FCSTD DOCUMENT  (FreeCAD 0.19R24366 (Git))
Label: Amplifier box insulating mounting flange
License: All rights reserved
LicenseURL: http://en.wikipedia.org/wiki/All_rights_reserved
objects: Sketcher::SketchObject×1, PartDesign::Body×1
note: 2 computed .brp shape members not serialized (recipe doc carries the construction recipe); baked Part::Feature solids carry a one-line shape summary decoded from their .brp

FEATURE [Sketcher::SketchObject] Sketch
  FullyConstrained = true
  MapMode = 5
  Support = -> [XY_Plane]
  sketch-geometry (27):
    g0: LineSegment StartX=-40 StartY=53.5 StartZ=0 EndX=-40 EndY=-53.5 EndZ=0
    g1: LineSegment StartX=40 StartY=53.5 StartZ=0 EndX=40 EndY=-53.5 EndZ=0
    g2: LineSegment StartX=-40 StartY=53.5 StartZ=0 EndX=40 EndY=53.5 EndZ=0
    g3: LineSegment StartX=-40 StartY=-53.5 StartZ=0 EndX=40 EndY=-53.5 EndZ=0
    g4: Circle CenterX=-22 CenterY=0 CenterZ=0 NormalX=0 NormalY=0 NormalZ=1 AngleXU=0 Radius=2.5
    g5: Circle CenterX=22 CenterY=0 CenterZ=0 NormalX=0 NormalY=0 NormalZ=1 AngleXU=0 Radius=2.5
    g6: Circle CenterX=0 CenterY=65 CenterZ=0 NormalX=0 NormalY=0 NormalZ=1 AngleXU=0 Radius=2.5
    g7: Circle CenterX=0 CenterY=-65 CenterZ=0 NormalX=0 NormalY=0 NormalZ=1 AngleXU=0 Radius=2.5
    g8: ArcOfCircle CenterX=0 CenterY=-65 CenterZ=0 NormalX=0 NormalY=0 NormalZ=1 AngleXU=0 Radius=10 StartAngle=4.25879 EndAngle=5.16599
    g9: ArcOfCircle CenterX=-35 CenterY=53.5 CenterZ=0 NormalX=0 NormalY=0 NormalZ=1 AngleXU=0 Radius=5 StartAngle=2.02439 EndAngle=3.14159
    g10: ArcOfCircle CenterX=35 CenterY=53.5 CenterZ=0 NormalX=0 NormalY=0 NormalZ=1 AngleXU=0 Radius=5 StartAngle=0 EndAngle=1.1172
    g11: ArcOfCircle CenterX=35 CenterY=-53.5 CenterZ=0 NormalX=0 NormalY=0 NormalZ=1 AngleXU=0 Radius=5 StartAngle=5.16599 EndAngle=6.28319
    g12: ArcOfCircle CenterX=-35 CenterY=-53.5 CenterZ=0 NormalX=0 NormalY=0 NormalZ=1 AngleXU=0 Radius=5 StartAngle=3.14159 EndAngle=4.25879
    g13: LineSegment StartX=-37.191 StartY=-57.9944 StartZ=0 EndX=-4.38202 EndY=-73.9888 EndZ=0
    g14: LineSegment StartX=37.191 StartY=-57.9944 StartZ=0 EndX=4.38202 EndY=-73.9888 EndZ=0
    g15: LineSegment StartX=37.191 StartY=57.9944 StartZ=0 EndX=4.38202 EndY=73.9888 EndZ=0
    g16: LineSegment StartX=-37.191 StartY=57.9944 StartZ=0 EndX=-4.38202 EndY=73.9888 EndZ=0
    g17: ArcOfCircle CenterX=0 CenterY=65 CenterZ=0 NormalX=0 NormalY=0 NormalZ=1 AngleXU=0 Radius=10 StartAngle=1.1172 EndAngle=2.02439
    g18: Circle CenterX=-30.353 CenterY=-36.598 CenterZ=0 NormalX=0 NormalY=0 NormalZ=1 AngleXU=0 Radius=4.5
    g19: Circle CenterX=30.353 CenterY=-36.598 CenterZ=0 NormalX=0 NormalY=0 NormalZ=1 AngleXU=0 Radius=4.5
    g20: Circle CenterX=-30.353 CenterY=31.728 CenterZ=0 NormalX=0 NormalY=0 NormalZ=1 AngleXU=0 Radius=4.5
    g21: Circle CenterX=30.353 CenterY=31.728 CenterZ=0 NormalX=0 NormalY=0 NormalZ=1 AngleXU=0 Radius=4.5
    g22: LineSegment StartX=-30.353 StartY=31.728 StartZ=0 EndX=30.353 EndY=31.728 EndZ=0
    g23: LineSegment StartX=30.353 StartY=-36.598 StartZ=0 EndX=-30.353 EndY=-36.598 EndZ=0
    g24: GeomPoint X=-30.353 Y=-2.435 Z=0
    g25: LineSegment StartX=-30.353 StartY=31.728 StartZ=0 EndX=-30.353 EndY=-36.598 EndZ=0
    g26: LineSegment StartX=30.353 StartY=-36.598 StartZ=0 EndX=30.353 EndY=31.728 EndZ=0
  constraints (61):
    c: Vertical(g1)
    c: Horizontal(g3)
    c: Symmetric(g2,g3,g-1)
    c: DistanceY(g3,g2) = 107
    c: PointOnObject(g4,g-1)
    c: Symmetric(g4,g5,g-2)
    c: Equal(g4,g5)
    c: PointOnObject(g6,g-2)
    c: Symmetric(g6,g7,g-1)
    c: DistanceX(g4,g5) = 44
    c: Diameter(g4) = 5
    c: Equal(g6,g4)
    c: Equal(g4,g7)
    c: DistanceY(g7,g6) = 130
    c: Coincident(g8,g7)
    c: Coincident(g0,g2)
    c: Coincident(g1,g2)
    c: Coincident(g1,g3)
    c: PointOnObject(g0,g3)
    c: Tangent(g9,g0) = -1.5708
    c: Tangent(g10,g1) = 1.5708
    c: Vertical(g0)
    c: Tangent(g11,g1) = 1.5708
    c: Tangent(g12,g0) = -1.5708
    c: Tangent(g8,g13) = -1.5708
    c: Tangent(g8,g14) = 1.5708
    c: Tangent(g17,g16) = 1.5708
    c: Tangent(g17,g15) = -1.5708
    c: Coincident(g17,g6)
    c: Tangent(g14,g11) = 1.5708
    c: Tangent(g13,g12) = -1.5708
    c: Equal(g12,g9)
    c: Equal(g9,g10)
    c: Equal(g10,g11)
    c: Radius(g9) = 5
    c: Tangent(g16,g9) = 1.5708
    c: Radius(g17) = 10
    c: Symmetric(g0,g1,g-2)
    c: DistanceX(g3,g3) = 80
    c: Tangent(g15,g10) = -1.5708
    c: Equal(g8,g17)
    c: Coincident(g22,g20)
    c: Coincident(g22,g21)
    c: Coincident(g23,g19)
    c: Coincident(g23,g18)
    c: Horizontal(g22)
    c: Symmetric(g18,g19,g-2)
    c: Equal(g20,g21)
    c: Equal(g21,g19)
    c: Equal(g19,g18)
    c: Diameter(g20) = 9
    c: Symmetric(g20,g18,g24)
    c: DistanceY(g24,g4) = 2.435
    c: Coincident(g25,g20)
    c: Coincident(g25,g18)
    c: Vertical(g25)
    c: Coincident(g26,g19)
    c: Coincident(g26,g21)
    c: Vertical(g26)
    c: DistanceX(g23,g23) = 60.706
    c: DistanceY(g25,g25) = 68.326
FEATURE [PartDesign::Body] Body
  Group = -> [Sketch]
  Origin = -> Origin
